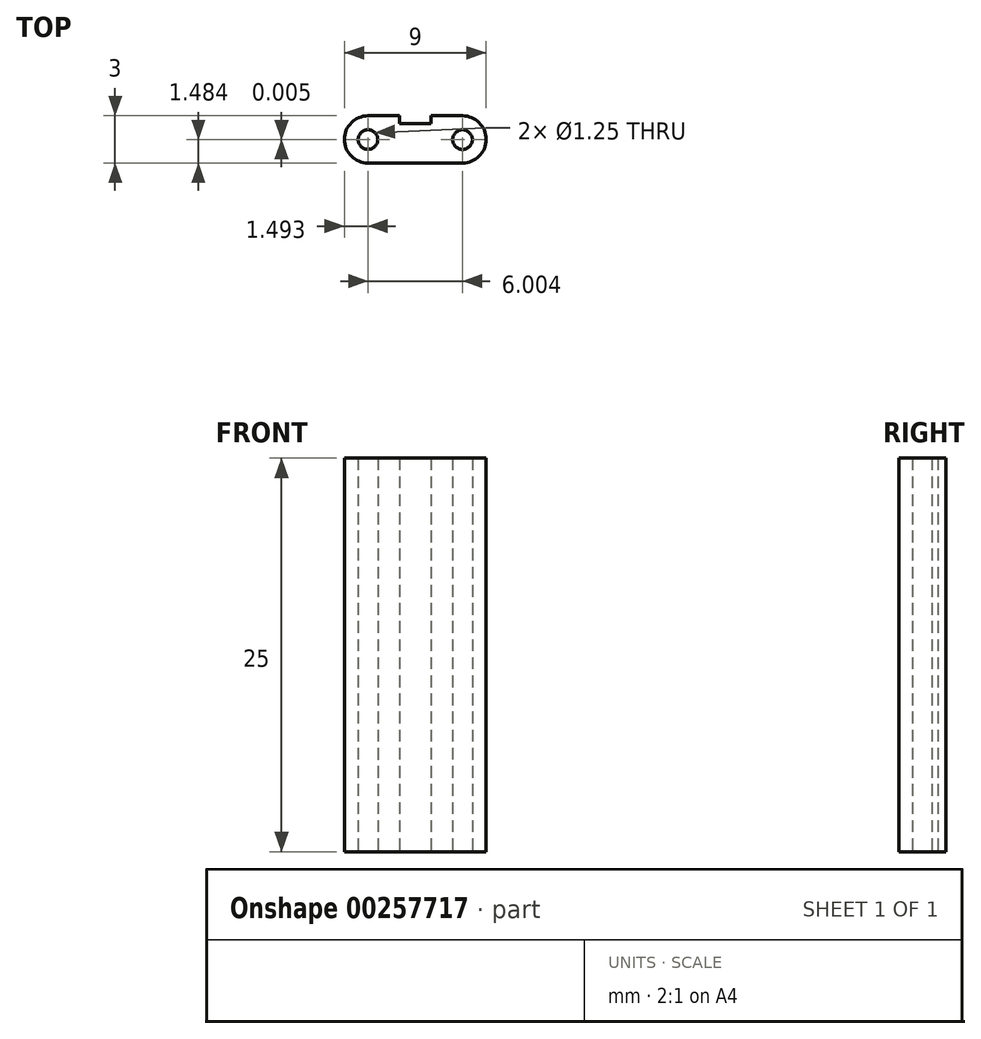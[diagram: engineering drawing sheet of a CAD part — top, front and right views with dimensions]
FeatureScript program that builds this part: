
annotation { "Feature Type Name" : "Feature", "Feature Type Description" : "" }
export const myFeature = defineFeature(function(context is Context, id is Id, definition is map)
    precondition{}
    {
        {
            var Q0;
            Q0=qCreatedBy(makeId("Top.planeOp"),FACE);
            var sketch = newSketch(context, id + "F0", { "sketchPlane" : qUnion([Q0])});
            skLineSegment(sketch, "E0", {"start": v(-5.82, -24.93) * mm, "end": v(0.18, -24.93) * mm});
            skLineSegment(sketch, "E1", {"start": v(-5.82, -21.93) * mm, "end": v(-3.82, -21.93) * mm});
            skLineSegment(sketch, "E2", {"start": v(0.18, -21.93) * mm, "end": v(-1.82, -21.93) * mm});
            skLineSegment(sketch, "E3", {"start": v(-3.82, -21.93) * mm, "end": v(-3.82, -22.43) * mm});
            skLineSegment(sketch, "E4", {"start": v(-3.82, -22.43) * mm, "end": v(-1.82, -22.43) * mm});
            skLineSegment(sketch, "E5", {"start": v(-1.82, -22.43) * mm, "end": v(-1.82, -21.93) * mm});
            skCircle(sketch, "E6", {"center": v(-5.83, -23.44) * mm, "radius": 0.62 * mm});
            skCircle(sketch, "E7", {"center": v(0.18, -23.45) * mm, "radius": 0.62 * mm});
            skArc(sketch, "E8", {"start": v(0.18, -24.93) * mm, "mid": v(1.68, -23.43) * mm, "end": v(0.18, -21.93) * mm});
            skArc(sketch, "E9", {"start": v(-5.82, -21.93) * mm, "mid": v(-7.32, -23.43) * mm, "end": v(-5.82, -24.93) * mm});
            skSolve(sketch);
        }
        {
            var Q0;
            Q0=makeQuery(id+"F0.imprint","IMPRINT",FACE,{"disambiguationData":[TD([[makeQuery(id+"F0.imprint","IMPRINT",EDGE,{"derivedFrom":sQuery(id+"F0.wireOp",EDGE,"E0")}),1.0]])]});
            extrude(context, id + "F1", {"entities" : qUnion([Q0]), "depth" : 25 * mm});
        }
    });
